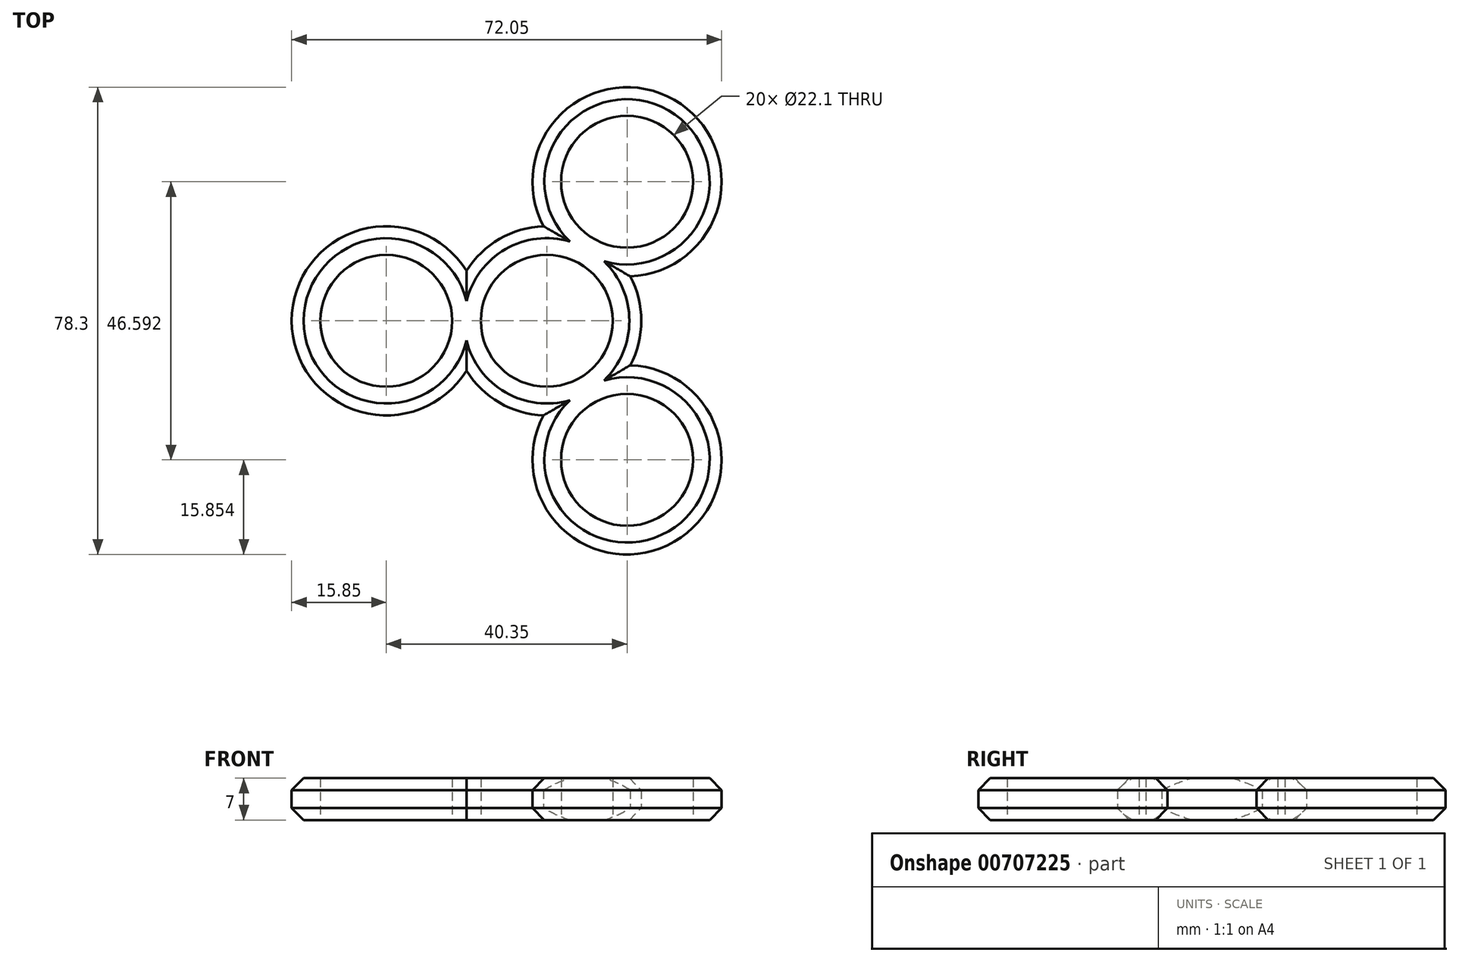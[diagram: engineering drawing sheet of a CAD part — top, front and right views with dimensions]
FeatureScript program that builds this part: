
annotation { "Feature Type Name" : "Feature", "Feature Type Description" : "" }
export const myFeature = defineFeature(function(context is Context, id is Id, definition is map)
    precondition{}
    {
        {
            var Q0;
            Q0=qCreatedBy(makeId("Top.planeOp"),FACE);
            var sketch = newSketch(context, id + "F0", { "sketchPlane" : qUnion([Q0])});
            skCircle(sketch, "E0", {"center": v(0, 0) * mm, "radius": 11.05 * mm});
            skCircle(sketch, "E1", {"center": v(0, 0) * mm, "radius": 42.75 * mm, "construction": true});
            skLineSegment(sketch, "E2", {"start": v(-11.05, 0) * mm, "end": v(-42.75, 0) * mm, "construction": true});
            skCircle(sketch, "E3", {"center": v(-26.9, 0) * mm, "radius": 11.05 * mm});
            skCircle(sketch, "E4", {"center": v(-26.9, 0) * mm, "radius": 15.85 * mm});
            skLineSegment(sketch, "E5", {"start": v(0, 0) * mm, "end": v(5.52, 9.57) * mm, "construction": true});
            skLineSegment(sketch, "E6", {"start": v(0, 0) * mm, "end": v(5.53, -9.57) * mm, "construction": true});
            skLineSegment(sketch, "E7", {"start": v(0, 0) * mm, "end": v(-11.05, 0) * mm, "construction": true});
            skLineSegment(sketch, "E8", {"start": v(5.52, 9.57) * mm, "end": v(21.37, 37.02) * mm, "construction": true});
            skLineSegment(sketch, "E9", {"start": v(5.53, -9.57) * mm, "end": v(21.38, -37.02) * mm, "construction": true});
            skCircle(sketch, "E10", {"center": v(0, 0) * mm, "radius": 15.85 * mm});
            skCircle(sketch, "E11", {"center": v(13.45, 23.3) * mm, "radius": 11.05 * mm});
            skCircle(sketch, "E12", {"center": v(13.45, 23.3) * mm, "radius": 15.85 * mm});
            skCircle(sketch, "E13", {"center": v(13.45, -23.3) * mm, "radius": 11.05 * mm});
            skCircle(sketch, "E14", {"center": v(13.45, -23.3) * mm, "radius": 15.85 * mm});
            skSolve(sketch);
        }
        {
            var Q0;
            {var subQ0=sQuery(id+"F0.wireOp",EDGE,"E3");Q0=makeQuery(id+"F0.imprint","IMPRINT",FACE,{"disambiguationData":[TD([[makeQuery(id+"F0.imprint","IMPRINT",EDGE,{"derivedFrom":subQ0}),-1.0]])]});}
            var Q1;
            {var subQ0=sQuery(id+"F0.wireOp",EDGE,"E10");var subQ1=sQuery(id+"F0.wireOp",EDGE,"E4");var subQ2=makeQuery(id+"F0.imprint","INTERSECT",VERTEX,{"disambiguationData":[OD(0.0)],"derivedFrom":[subQ1,subQ0]});Q1=makeQuery(id+"F0.imprint","IMPRINT",FACE,{"disambiguationData":[TD([[makeQuery(id+"F0.imprint","IMPRINT",EDGE,{"disambiguationData":[TD([[subQ2,1.0]])],"derivedFrom":subQ1}),1.0]])]});}
            var Q2;
            {var subQ0=sQuery(id+"F0.wireOp",EDGE,"E4");var subQ1=sQuery(id+"F0.wireOp",EDGE,"E0");var subQ2=makeQuery(id+"F0.imprint","INTERSECT",VERTEX,{"derivedFrom":[subQ1,subQ0]});Q2=makeQuery(id+"F0.imprint","IMPRINT",FACE,{"disambiguationData":[TD([[makeQuery(id+"F0.imprint","IMPRINT",EDGE,{"disambiguationData":[TD([[subQ2,1.0]])],"derivedFrom":subQ1}),-1.0]])]});}
            var Q3;
            {var subQ0=sQuery(id+"F0.wireOp",EDGE,"E4");var subQ1=sQuery(id+"F0.wireOp",EDGE,"E0");var subQ2=makeQuery(id+"F0.imprint","INTERSECT",VERTEX,{"derivedFrom":[subQ1,subQ0]});Q3=makeQuery(id+"F0.imprint","IMPRINT",FACE,{"disambiguationData":[TD([[makeQuery(id+"F0.imprint","IMPRINT",EDGE,{"disambiguationData":[TD([[subQ2,-1.0]])],"derivedFrom":subQ1}),-1.0]])]});}
            var Q4;
            {var subQ0=sQuery(id+"F0.wireOp",EDGE,"E14");var subQ1=sQuery(id+"F0.wireOp",EDGE,"E10");var subQ2=makeQuery(id+"F0.imprint","INTERSECT",VERTEX,{"disambiguationData":[OD(0.0)],"derivedFrom":[subQ1,subQ0]});Q4=makeQuery(id+"F0.imprint","IMPRINT",FACE,{"disambiguationData":[TD([[makeQuery(id+"F0.imprint","IMPRINT",EDGE,{"disambiguationData":[TD([[subQ2,-1.0]])],"derivedFrom":subQ1}),1.0]])]});}
            var Q5;
            {var subQ0=sQuery(id+"F0.wireOp",EDGE,"E12");var subQ1=sQuery(id+"F0.wireOp",EDGE,"E0");var subQ2=makeQuery(id+"F0.imprint","INTERSECT",VERTEX,{"derivedFrom":[subQ1,subQ0]});Q5=makeQuery(id+"F0.imprint","IMPRINT",FACE,{"disambiguationData":[TD([[makeQuery(id+"F0.imprint","IMPRINT",EDGE,{"disambiguationData":[TD([[subQ2,1.0]])],"derivedFrom":subQ1}),-1.0]])]});}
            var Q6;
            {var subQ0=sQuery(id+"F0.wireOp",EDGE,"E11");Q6=makeQuery(id+"F0.imprint","IMPRINT",FACE,{"disambiguationData":[TD([[makeQuery(id+"F0.imprint","IMPRINT",EDGE,{"derivedFrom":subQ0}),-1.0]])]});}
            var Q7;
            {var subQ0=sQuery(id+"F0.wireOp",EDGE,"E10");var subQ1=makeQuery(id+"F0.imprint","INTERSECT",VERTEX,{"derivedFrom":[subQ0,sQuery(id+"F0.wireOp",EDGE,"E11")]});Q7=makeQuery(id+"F0.imprint","IMPRINT",FACE,{"disambiguationData":[TD([[makeQuery(id+"F0.imprint","IMPRINT",EDGE,{"disambiguationData":[TD([[subQ1,1.0]])],"derivedFrom":subQ0}),1.0]])]});}
            var Q8;
            {var subQ3=sQuery(id+"F0.wireOp",EDGE,"E13");Q8=makeQuery(id+"F0.imprint","IMPRINT",FACE,{"disambiguationData":[TD([[makeQuery(id+"F0.imprint","IMPRINT",EDGE,{"derivedFrom":subQ3}),-1.0]])]});}
            extrude(context, id + "F1", {"entities" : qUnion([Q0, Q1, Q2, Q3, Q4, Q5, Q6, Q7, Q8]), "depth" : 7 * mm, "offsetDistance" : 25 * mm});
        }
        {
            var Q0;
            Q0=makeQuery(id+"F1.opExtrude","CAP_EDGE",EDGE,{"disambiguationData":[OSD([sQuery(id+"F0.wireOp",EDGE,"E4")])],"isStart":false});
            var Q1;
            {var subQ0=sQuery(id+"F0.wireOp",EDGE,"E10");Q1=makeQuery(id+"F1.opExtrude","CAP_EDGE",EDGE,{"disambiguationData":[OSD([subQ0]),TDD([makeQuery(id+"F0.imprint","IMPRINT",EDGE,{"disambiguationData":[TD([[makeQuery(id+"F0.imprint","INTERSECT",VERTEX,{"disambiguationData":[OD(1.0)],"derivedFrom":[sQuery(id+"F0.wireOp",EDGE,"E4"),subQ0]}),-1.0]])],"derivedFrom":subQ0})])],"isStart":false});}
            var Q2;
            Q2=makeQuery(id+"F1.opExtrude","CAP_EDGE",EDGE,{"disambiguationData":[OSD([sQuery(id+"F0.wireOp",EDGE,"E14")])],"isStart":false});
            var Q3;
            {var subQ0=sQuery(id+"F0.wireOp",EDGE,"E10");Q3=makeQuery(id+"F1.opExtrude","CAP_EDGE",EDGE,{"disambiguationData":[OSD([subQ0]),TDD([makeQuery(id+"F0.imprint","IMPRINT",EDGE,{"disambiguationData":[TD([[makeQuery(id+"F0.imprint","INTERSECT",VERTEX,{"disambiguationData":[OD(0.0)],"derivedFrom":[subQ0,sQuery(id+"F0.wireOp",EDGE,"E12")]}),1.0]])],"derivedFrom":subQ0})])],"isStart":false});}
            var Q4;
            Q4=makeQuery(id+"F1.opExtrude","CAP_EDGE",EDGE,{"disambiguationData":[OSD([sQuery(id+"F0.wireOp",EDGE,"E12")])],"isStart":false});
            var Q5;
            {var subQ0=sQuery(id+"F0.wireOp",EDGE,"E10");Q5=makeQuery(id+"F1.opExtrude","CAP_EDGE",EDGE,{"disambiguationData":[OSD([subQ0]),TDD([makeQuery(id+"F0.imprint","IMPRINT",EDGE,{"disambiguationData":[TD([[makeQuery(id+"F0.imprint","INTERSECT",VERTEX,{"disambiguationData":[OD(0.0)],"derivedFrom":[sQuery(id+"F0.wireOp",EDGE,"E4"),subQ0]}),1.0]])],"derivedFrom":subQ0})])],"isStart":false});}
            var Q6;
            Q6=makeQuery(id+"F1.opExtrude","CAP_EDGE",EDGE,{"disambiguationData":[OSD([sQuery(id+"F0.wireOp",EDGE,"E4")])],"isStart":true});
            var Q7;
            {var subQ0=sQuery(id+"F0.wireOp",EDGE,"E10");Q7=makeQuery(id+"F1.opExtrude","CAP_EDGE",EDGE,{"disambiguationData":[OSD([subQ0]),TDD([makeQuery(id+"F0.imprint","IMPRINT",EDGE,{"disambiguationData":[TD([[makeQuery(id+"F0.imprint","INTERSECT",VERTEX,{"disambiguationData":[OD(1.0)],"derivedFrom":[sQuery(id+"F0.wireOp",EDGE,"E4"),subQ0]}),-1.0]])],"derivedFrom":subQ0})])],"isStart":true});}
            var Q8;
            Q8=makeQuery(id+"F1.opExtrude","CAP_EDGE",EDGE,{"disambiguationData":[OSD([sQuery(id+"F0.wireOp",EDGE,"E14")])],"isStart":true});
            var Q9;
            Q9=makeQuery(id+"F1.opExtrude","CAP_EDGE",EDGE,{"disambiguationData":[OSD([sQuery(id+"F0.wireOp",EDGE,"E12")])],"isStart":true});
            var Q10;
            {var subQ0=sQuery(id+"F0.wireOp",EDGE,"E10");Q10=makeQuery(id+"F1.opExtrude","CAP_EDGE",EDGE,{"disambiguationData":[OSD([subQ0]),TDD([makeQuery(id+"F0.imprint","IMPRINT",EDGE,{"disambiguationData":[TD([[makeQuery(id+"F0.imprint","INTERSECT",VERTEX,{"disambiguationData":[OD(0.0)],"derivedFrom":[subQ0,sQuery(id+"F0.wireOp",EDGE,"E12")]}),1.0]])],"derivedFrom":subQ0})])],"isStart":true});}
            var Q11;
            {var subQ0=sQuery(id+"F0.wireOp",EDGE,"E10");Q11=makeQuery(id+"F1.opExtrude","CAP_EDGE",EDGE,{"disambiguationData":[OSD([subQ0]),TDD([makeQuery(id+"F0.imprint","IMPRINT",EDGE,{"disambiguationData":[TD([[makeQuery(id+"F0.imprint","INTERSECT",VERTEX,{"disambiguationData":[OD(0.0)],"derivedFrom":[sQuery(id+"F0.wireOp",EDGE,"E4"),subQ0]}),1.0]])],"derivedFrom":subQ0})])],"isStart":true});}
            chamfer(context, id + "F2", {"entities" : qUnion([Q0, Q1, Q2, Q3, Q4, Q5, Q6, Q7, Q8, Q9, Q10, Q11]), "chamferType" : ChamferType.TWO_OFFSETS, "width1" : 2 * mm, "oppositeDirection" : true, "width2" : 2 * mm, "tangentPropagation" : true});
        }
    });
